# Revit family: Shower_Arm-GROHE-Relexa-26633000
name_source: partatom
category: Plumbing Fixtures
revit_build: Autodesk Revit 2018 (Build: 20170223_1515(x64)
units: mm (PartAtom-declared; Revit-internal decimal feet)

## family parameters
Cut with Voids When Loaded = No
Host = Face
OmniClass Number = 23.45.05.14.17
OmniClass Title = Showers
Part Type = Normal
Room Calculation Point = No
Round Connector Dimension = Use Diameter
Shared = Yes

## types (1)
- 26633000
    48118000 Escutcheon = Yes
    Assembly Code = D2010710
    CW Connection = No
    CWFU = 4
    Default Elevation = 0"
    Description = Relexa 6 in. Shower Arm
    Finish = Brass-Grohe-000-StarLight Chrome
    HW Connection = No
    HWFU = 3
    IAPMO Compliance = ASME A112.18.1/CSA B125.1
    Installation Type = Wall Mounted
    Length = 6"
    Manufacturer = Grohe
    Material = Brass-Grohe-000-StarLight Chrome
    Model = 26633000
    Product Documentation Link = https://americanstandard.box.com
    Product Page URL = https://www.grohe.us
    Tempered Connection Diameter = 1/2"
    Tempered Water Connection = Yes
    URL = https://www.grohe.us
    Vent Connection = No
    WFU = 3
    Waste Connection = No
    Width = 2 9/16"
    cUPC Compliant = Yes

## geometry (parser evidence)
native form markers: Sweep x3
no freeform markers — native parametric forms only
